# Revit family: Kanalunterteil
name_source: partatom
category: Generic Models
revit_build: Autodesk Revit 2017 (Build: 20190508_0315(x64)
units: mm (PartAtom-declared; Revit-internal decimal feet)

## family parameters
Always vertical = Yes
Can host rebar = No
Cut with Voids When Loaded = No
Part Type = Normal
Room Calculation Point = No
Round Connector Dimension = Use Diameter
Shared = No
Work Plane-Based = No

## types (1)
- AIKU 25040
    Article Type = AIKU 25040
    Cut's number = 2
    Cut's number 2 = 9
    GTIN = 4012195100737
    Height = 35 mm
    Length = 2399 mm  [stored 7.87073 ft]
    Manufacturer = Obo Bettermann
    Manufacturer Art.No. = 7404712
    Material = Strip-galvanised
    URL = http://www.obo-bettermann.com
    Width = 150 mm
    Width 1 = 75 mm  [stored 0.246063 ft]

note: [stored X ft] marks values corroborated as IEEE doubles in the binary element streams (Revit-internal decimal feet)

## geometry (parser evidence)
native form markers: Sweep x2
no freeform markers — native parametric forms only
